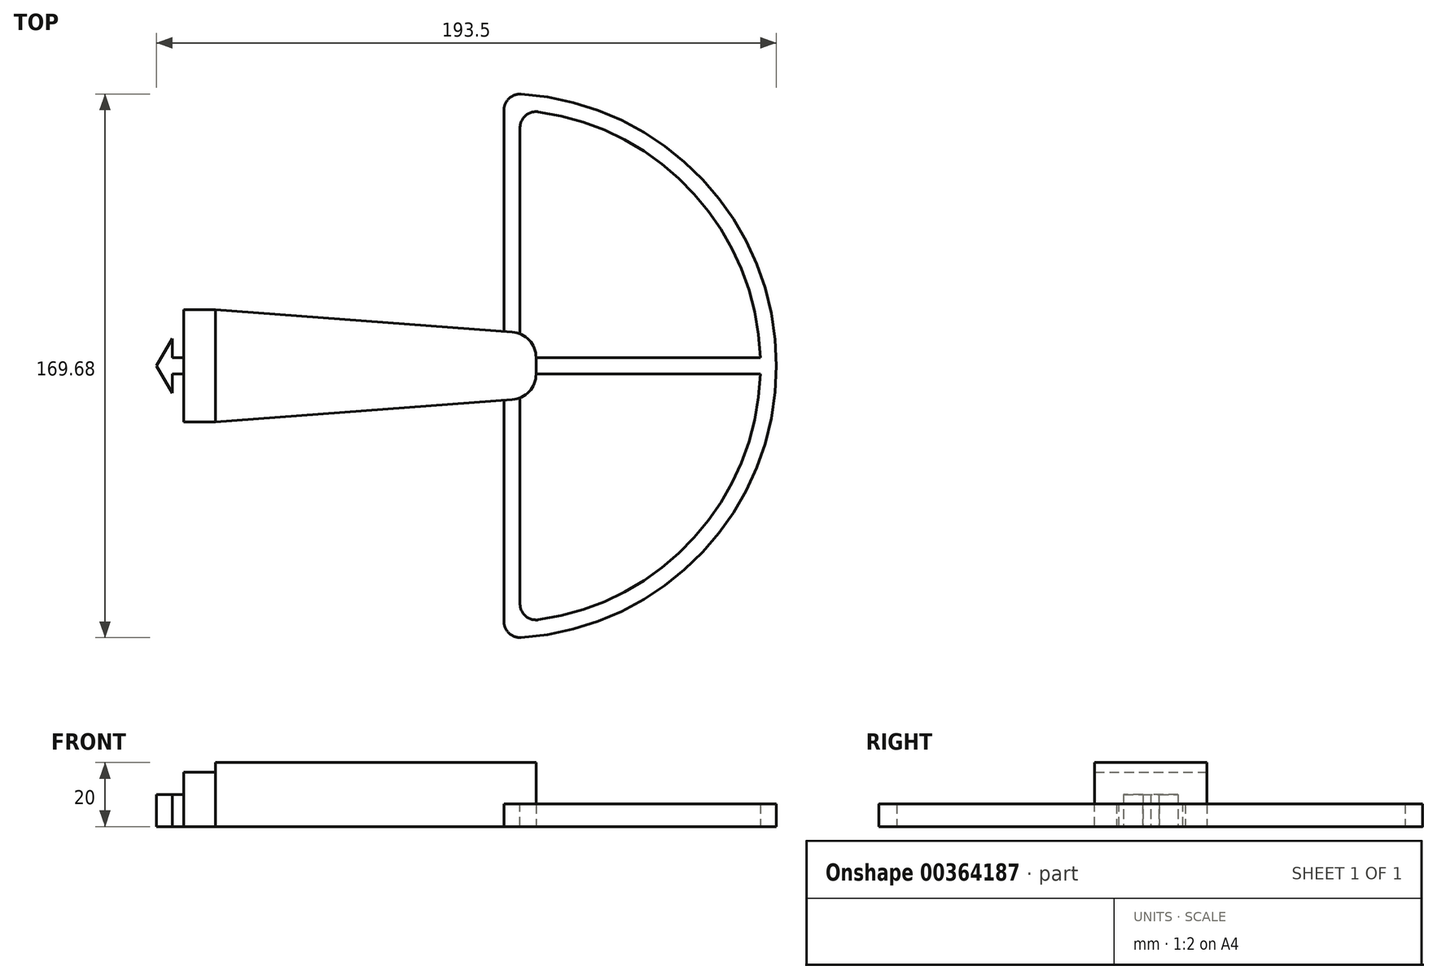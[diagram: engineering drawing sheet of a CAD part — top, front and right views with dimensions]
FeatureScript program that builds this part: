
annotation { "Feature Type Name" : "Feature", "Feature Type Description" : "" }
export const myFeature = defineFeature(function(context is Context, id is Id, definition is map)
    precondition{}
    {
        {
            var Q0;
            Q0=qCreatedBy(makeId("Top.planeOp"),FACE);
            var sketch = newSketch(context, id + "F0", { "sketchPlane" : qUnion([Q0])});
            skLineSegment(sketch, "E0.bottom", {"start": v(55, -17.5) * mm, "end": v(-55, -17.5) * mm});
            skLineSegment(sketch, "E0.top", {"start": v(55, 17.5) * mm, "end": v(-55, 17.5) * mm});
            skLineSegment(sketch, "E0.left", {"start": v(55, -17.5) * mm, "end": v(55, 17.5) * mm});
            skLineSegment(sketch, "E0.right", {"start": v(-55, -17.5) * mm, "end": v(-55, 17.5) * mm});
            skPoint(sketch, "E0.middle", {"position": v(0, 0) * mm});
            skLineSegment(sketch, "E1.bottom", {"start": v(-55, -2.5) * mm, "end": v(-58.5, -2.5) * mm});
            skLineSegment(sketch, "E1.top", {"start": v(-55, 2.5) * mm, "end": v(-58.5, 2.5) * mm});
            skLineSegment(sketch, "E1.left", {"start": v(-55, -2.5) * mm, "end": v(-55, 2.5) * mm});
            skLineSegment(sketch, "E1.right", {"start": v(-58.5, -2.5) * mm, "end": v(-58.5, 2.5) * mm});
            skPoint(sketch, "E1.middle", {"position": v(-56.75, 0) * mm});
            skPoint(sketch, "E2", {"position": v(-58.5, 8.5) * mm});
            skPoint(sketch, "E3", {"position": v(-58.5, -8.5) * mm});
            skPoint(sketch, "E4", {"position": v(-58.5, 0) * mm});
            skLineSegment(sketch, "E5", {"start": v(-58.5, 0) * mm, "end": v(-58.5, 8.5) * mm});
            skLineSegment(sketch, "E6", {"start": v(-58.5, 0) * mm, "end": v(-58.5, -8.5) * mm});
            skPoint(sketch, "E7", {"position": v(-63.5, 0) * mm});
            skLineSegment(sketch, "E8", {"start": v(-58.5, 8.5) * mm, "end": v(-63.5, 0) * mm});
            skLineSegment(sketch, "E9", {"start": v(-58.5, -8.5) * mm, "end": v(-63.5, 0) * mm});
            skSolve(sketch);
        }
        {
            var Q0;
            {var subQ6=sQuery(id+"F0.wireOp",EDGE,"E8");Q0=makeQuery(id+"F0.imprint","IMPRINT",FACE,{"disambiguationData":[TD([[makeQuery(id+"F0.imprint","IMPRINT",EDGE,{"derivedFrom":subQ6}),1.0]])]});}
            var Q1;
            {var subQ4=sQuery(id+"F0.wireOp",EDGE,"E1.bottom");Q1=makeQuery(id+"F0.imprint","IMPRINT",FACE,{"disambiguationData":[TD([[makeQuery(id+"F0.imprint","IMPRINT",EDGE,{"derivedFrom":subQ4}),-1.0]])]});}
            extrude(context, id + "F1", {"entities" : qUnion([Q0, Q1]), "depth" : 10 * mm});
        }
        {
            var Q0;
            {var subQ1=sQuery(id+"F0.wireOp",EDGE,"E0.bottom");Q0=makeQuery(id+"F0.imprint","IMPRINT",FACE,{"disambiguationData":[TD([[makeQuery(id+"F0.imprint","IMPRINT",EDGE,{"derivedFrom":subQ1}),-1.0]])]});}
            extrude(context, id + "F2", {"entities" : qUnion([Q0]), "operationType" : NewBodyOperationType.ADD, "depth" : 17 * mm});
        }
        {
            var Q0;
            Q0=makeQuery(id+"F2.opExtrude","CAP_FACE",FACE,{"disambiguationData":[OSD([sQuery(id+"F0.wireOp",EDGE,"E0.bottom"),sQuery(id+"F0.wireOp",EDGE,"E0.top"),sQuery(id+"F0.wireOp",EDGE,"E0.left"),sQuery(id+"F0.wireOp",EDGE,"E0.right"),sQuery(id+"F0.wireOp",EDGE,"E1.left")])],"isStart":false});
            var sketch = newSketch(context, id + "F3", { "sketchPlane" : qUnion([Q0])});
            skLineSegment(sketch, "E10.bottom", {"start": v(55, 17.5) * mm, "end": v(-45, 17.5) * mm});
            skLineSegment(sketch, "E10.top", {"start": v(55, -17.5) * mm, "end": v(-45, -17.5) * mm});
            skLineSegment(sketch, "E10.left", {"start": v(55, 17.5) * mm, "end": v(55, -17.5) * mm});
            skLineSegment(sketch, "E10.right", {"start": v(-45, 17.5) * mm, "end": v(-45, -17.5) * mm});
            skSolve(sketch);
        }
        {
            var Q0;
            Q0=makeQuery(id+"F3.imprint","IMPRINT",FACE,{"disambiguationData":[TD([[makeQuery(id+"F3.imprint","IMPRINT",EDGE,{"derivedFrom":sQuery(id+"F3.wireOp",EDGE,"E10.bottom")}),1.0]])]});
            extrude(context, id + "F4", {"entities" : qUnion([Q0]), "operationType" : NewBodyOperationType.ADD, "depth" : 3 * mm});
        }
        {
            var Q0;
            Q0=makeQuery(id+"F4.boolean.opBoolean","MERGE",EDGE,{"derivedFrom":[makeQuery(id+"F2.opExtrude","SWEPT_EDGE",EDGE,{"disambiguationData":[OSD([sQuery(id+"F0.wireOp",EDGE,"E0.bottom"),sQuery(id+"F0.wireOp",EDGE,"E0.left")])]}),makeQuery(id+"F4.opExtrude","SWEPT_EDGE",EDGE,{"disambiguationData":[OSD([sQuery(id+"F3.wireOp",EDGE,"E10.top"),sQuery(id+"F3.wireOp",EDGE,"E10.left")])]})]});
            var Q1;
            Q1=makeQuery(id+"F4.boolean.opBoolean","MERGE",EDGE,{"derivedFrom":[makeQuery(id+"F2.opExtrude","SWEPT_EDGE",EDGE,{"disambiguationData":[OSD([sQuery(id+"F0.wireOp",EDGE,"E0.top"),sQuery(id+"F0.wireOp",EDGE,"E0.left")])]}),makeQuery(id+"F4.opExtrude","SWEPT_EDGE",EDGE,{"disambiguationData":[OSD([sQuery(id+"F3.wireOp",EDGE,"E10.bottom"),sQuery(id+"F3.wireOp",EDGE,"E10.left")])]})]});
            chamfer(context, id + "F5", {"entities" : qUnion([Q0, Q1]), "chamferType" : ChamferType.TWO_OFFSETS, "width1" : 7.5 * mm, "oppositeDirection" : false, "width2" : 100 * mm, "tangentPropagation" : true});
        }
        {
            var Q0;
            {var subQ0=sQuery(id+"F3.wireOp",EDGE,"E10.left");var subQ1=sQuery(id+"F0.wireOp",EDGE,"E0.left");Q0=makeQuery(id+"F5.opChamfer","BLEND_EDGE",EDGE,{"blendedFrom":[makeQuery(id+"F4.boolean.opBoolean","MERGE",EDGE,{"derivedFrom":[makeQuery(id+"F2.opExtrude","SWEPT_EDGE",EDGE,{"disambiguationData":[OSD([sQuery(id+"F0.wireOp",EDGE,"E0.bottom"),subQ1])]}),makeQuery(id+"F4.opExtrude","SWEPT_EDGE",EDGE,{"disambiguationData":[OSD([sQuery(id+"F3.wireOp",EDGE,"E10.top"),subQ0])]})]}),makeQuery(id+"F4.boolean.opBoolean","MERGE",FACE,{"derivedFrom":[makeQuery(id+"F2.opExtrude","SWEPT_FACE",FACE,{"disambiguationData":[OSD([subQ1])]}),makeQuery(id+"F4.opExtrude","SWEPT_FACE",FACE,{"disambiguationData":[OSD([subQ0])]})]})],"blendedInto":[makeQuery(id+"F4.boolean.opBoolean","MERGE",FACE,{"derivedFrom":[makeQuery(id+"F2.opExtrude","SWEPT_FACE",FACE,{"disambiguationData":[OSD([subQ1])]}),makeQuery(id+"F4.opExtrude","SWEPT_FACE",FACE,{"disambiguationData":[OSD([subQ0])]})]})]});}
            var Q1;
            {var subQ0=sQuery(id+"F3.wireOp",EDGE,"E10.left");var subQ1=sQuery(id+"F0.wireOp",EDGE,"E0.left");Q1=makeQuery(id+"F5.opChamfer","BLEND_EDGE",EDGE,{"blendedFrom":[makeQuery(id+"F4.boolean.opBoolean","MERGE",EDGE,{"derivedFrom":[makeQuery(id+"F2.opExtrude","SWEPT_EDGE",EDGE,{"disambiguationData":[OSD([sQuery(id+"F0.wireOp",EDGE,"E0.top"),subQ1])]}),makeQuery(id+"F4.opExtrude","SWEPT_EDGE",EDGE,{"disambiguationData":[OSD([sQuery(id+"F3.wireOp",EDGE,"E10.bottom"),subQ0])]})]}),makeQuery(id+"F4.boolean.opBoolean","MERGE",FACE,{"derivedFrom":[makeQuery(id+"F2.opExtrude","SWEPT_FACE",FACE,{"disambiguationData":[OSD([subQ1])]}),makeQuery(id+"F4.opExtrude","SWEPT_FACE",FACE,{"disambiguationData":[OSD([subQ0])]})]})],"blendedInto":[makeQuery(id+"F4.boolean.opBoolean","MERGE",FACE,{"derivedFrom":[makeQuery(id+"F2.opExtrude","SWEPT_FACE",FACE,{"disambiguationData":[OSD([subQ1])]}),makeQuery(id+"F4.opExtrude","SWEPT_FACE",FACE,{"disambiguationData":[OSD([subQ0])]})]})]});}
            fillet(context, id + "F6", {"entities" : qUnion([Q0, Q1]), "radius" : 8 * mm, "tangentPropagation" : true, "allowEdgeOverflow" : false});
        }
        {
            var Q0;
            {var subQ1=sQuery(id+"F0.wireOp",EDGE,"E0.bottom");Q0=makeQuery(id+"F0.imprint","IMPRINT",FACE,{"disambiguationData":[TD([[makeQuery(id+"F0.imprint","IMPRINT",EDGE,{"derivedFrom":subQ1}),-1.0]])]});}
            var sketch = newSketch(context, id + "F7", { "sketchPlane" : qUnion([Q0])});
            skPoint(sketch, "E11", {"position": v(45, 0) * mm});
            skArc(sketch, "E12", {"start": v(50.31, 84.83) * mm, "mid": v(130, 0) * mm, "end": v(50.31, -84.83) * mm});
            skLineSegment(sketch, "E13", {"start": v(45, -79.84) * mm, "end": v(45, 79.84) * mm});
            skLineSegment(sketch, "E14", {"start": v(45, 0) * mm, "end": v(118.61, -42.5) * mm});
            skLineSegment(sketch, "E15", {"start": v(45, 0) * mm, "end": v(118.61, 42.5) * mm});
            skArc(sketch, "E16.0", {"start": v(55.67, 79.29) * mm, "mid": v(125, 0) * mm, "end": v(55.67, -79.29) * mm});
            skLineSegment(sketch, "E16.1", {"start": v(50, -74.33) * mm, "end": v(50, 74.33) * mm});
            skLineSegment(sketch, "E17.0", {"start": v(55, 0) * mm, "end": v(121.11, 38.17) * mm});
            skLineSegment(sketch, "E17.1", {"start": v(55, 0) * mm, "end": v(121.11, -38.17) * mm});
            skPoint(sketch, "E18.visualSharp", {"position": v(45, -85) * mm});
            skArc(sketch, "E18.filletArc", {"start": v(45, -79.84) * mm, "mid": v(46.58, -83.49) * mm, "end": v(50.31, -84.83) * mm});
            skPoint(sketch, "E19.visualSharp", {"position": v(45, 85) * mm});
            skArc(sketch, "E19.filletArc", {"start": v(50.31, 84.83) * mm, "mid": v(46.58, 83.49) * mm, "end": v(45, 79.84) * mm});
            skArc(sketch, "E20.filletArc", {"start": v(50, -74.33) * mm, "mid": v(51.7, -78.1) * mm, "end": v(55.67, -79.29) * mm});
            skArc(sketch, "E21.filletArc", {"start": v(55.67, 79.29) * mm, "mid": v(51.7, 78.1) * mm, "end": v(50, 74.33) * mm});
            skSolve(sketch);
        }
        {
            var Q0;
            Q0 = qSketchRegion(id + "F7", true);
            extrude(context, id + "F8", {"entities" : qUnion([Q0]), "operationType" : NewBodyOperationType.ADD, "depth" : 7 * mm});
        }
        {
            var Q0;
            Q0=makeQuery(id+"F4.boolean.opBoolean","MERGE",FACE,{"derivedFrom":[makeQuery(id+"F2.opExtrude","SWEPT_FACE",FACE,{"disambiguationData":[OSD([sQuery(id+"F0.wireOp",EDGE,"E0.left")])]}),makeQuery(id+"F4.opExtrude","SWEPT_FACE",FACE,{"disambiguationData":[OSD([sQuery(id+"F3.wireOp",EDGE,"E10.left")])]})]});
            var sketch = newSketch(context, id + "F9", { "sketchPlane" : qUnion([Q0])});
            skLineSegment(sketch, "E22.bottom", {"start": v(-2.58, 0) * mm, "end": v(2.58, 0) * mm});
            skLineSegment(sketch, "E22.top", {"start": v(-2.58, 7) * mm, "end": v(2.58, 7) * mm});
            skLineSegment(sketch, "E22.left", {"start": v(-2.58, 0) * mm, "end": v(-2.58, 7) * mm});
            skLineSegment(sketch, "E22.right", {"start": v(2.58, 0) * mm, "end": v(2.58, 7) * mm});
            skSolve(sketch);
        }
        {
            var Q0;
            Q0=makeQuery(id+"F9.imprint","IMPRINT",FACE,{"disambiguationData":[TD([[makeQuery(id+"F9.imprint","IMPRINT",EDGE,{"derivedFrom":sQuery(id+"F9.wireOp",EDGE,"E22.bottom")}),1.0]])]});
            extrude(context, id + "F10", {"entities" : qUnion([Q0]), "operationType" : NewBodyOperationType.ADD, "endBound" : BoundingType.UP_TO_NEXT, "depth" : 25 * mm});
        }
    });
